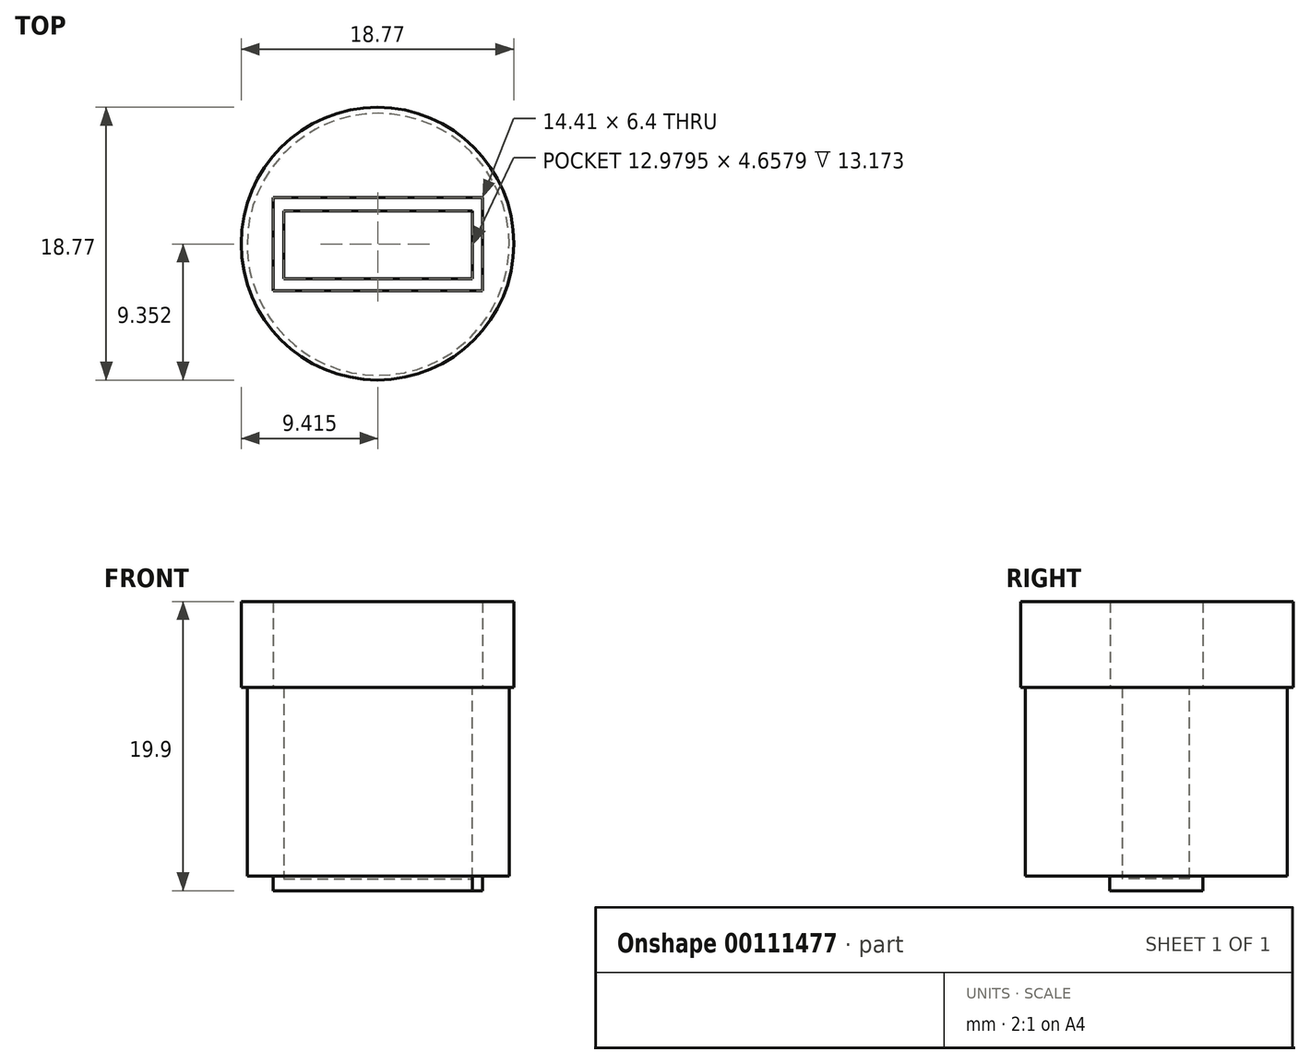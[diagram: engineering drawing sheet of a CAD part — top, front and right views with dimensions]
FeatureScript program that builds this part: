
annotation { "Feature Type Name" : "Feature", "Feature Type Description" : "" }
export const myFeature = defineFeature(function(context is Context, id is Id, definition is map)
    precondition{}
    {
        {
            var Q0;
            Q0=qCreatedBy(makeId("Top.planeOp"),FACE);
            var sketch = newSketch(context, id + "F0", { "sketchPlane" : qUnion([Q0])});
            skLineSegment(sketch, "E0.bottom", {"start": v(0, 0) * mm, "end": v(-14.41, 0) * mm});
            skLineSegment(sketch, "E0.top", {"start": v(0, -6.4) * mm, "end": v(-14.41, -6.4) * mm});
            skLineSegment(sketch, "E0.left", {"start": v(0, 0) * mm, "end": v(0, -6.4) * mm});
            skLineSegment(sketch, "E0.right", {"start": v(-14.41, 0) * mm, "end": v(-14.41, -6.4) * mm});
            skSolve(sketch);
        }
        {
            var Q0;
            Q0=makeQuery(id+"F0.imprint","IMPRINT",FACE,{"disambiguationData":[TD([[makeQuery(id+"F0.imprint","IMPRINT",EDGE,{"derivedFrom":sQuery(id+"F0.wireOp",EDGE,"E0.bottom")}),1.0]])]});
            var sketch = newSketch(context, id + "F1", { "sketchPlane" : qUnion([Q0])});
            skCircle(sketch, "E1", {"center": v(-7.23, -3.16) * mm, "radius": 9.39 * mm});
            skSolve(sketch);
        }
        {
            var Q0;
            Q0=makeQuery(id+"F1.imprint","IMPRINT",FACE,{"disambiguationData":[TD([[makeQuery(id+"F1.imprint","IMPRINT",EDGE,{"derivedFrom":sQuery(id+"F1.wireOp",EDGE,"E1")}),1.0]])]});
            extrude(context, id + "F2", {"entities" : qUnion([Q0]), "depth" : 5.9 * mm});
        }
        {
            var Q0;
            Q0=makeQuery(id+"F2.opExtrude","CAP_FACE",FACE,{"disambiguationData":[OSD([sQuery(id+"F0.wireOp",EDGE,"E0.bottom"),sQuery(id+"F0.wireOp",EDGE,"E0.top"),sQuery(id+"F0.wireOp",EDGE,"E0.left"),sQuery(id+"F0.wireOp",EDGE,"E0.right"),sQuery(id+"F1.wireOp",EDGE,"E1")])],"isStart":true});
            var sketch = newSketch(context, id + "F3", { "sketchPlane" : qUnion([Q0])});
            skLineSegment(sketch, "E2.bottom", {"start": v(0, 0) * mm, "end": v(-14.41, 0) * mm});
            skLineSegment(sketch, "E2.top", {"start": v(0, 0.92) * mm, "end": v(-14.41, 0.92) * mm});
            skLineSegment(sketch, "E2.left", {"start": v(0, 0) * mm, "end": v(0, 0.92) * mm});
            skLineSegment(sketch, "E2.right", {"start": v(-14.41, 0) * mm, "end": v(-14.41, 0.92) * mm});
            skSolve(sketch);
        }
        {
            var Q0;
            Q0=makeQuery(id+"F0.imprint","IMPRINT",FACE,{"disambiguationData":[TD([[makeQuery(id+"F0.imprint","IMPRINT",EDGE,{"derivedFrom":sQuery(id+"F0.wireOp",EDGE,"E0.bottom")}),1.0]])]});
            var sketch = newSketch(context, id + "F4", { "sketchPlane" : qUnion([Q0])});
            skCircle(sketch, "E3", {"center": v(-7.19, -3.2) * mm, "radius": 9.02 * mm});
            skSolve(sketch);
        }
        {
            var Q0;
            Q0=makeQuery(id+"F4.imprint","IMPRINT",FACE,{"disambiguationData":[TD([[makeQuery(id+"F4.imprint","IMPRINT",EDGE,{"derivedFrom":sQuery(id+"F4.wireOp",EDGE,"E3")}),1.0]])]});
            extrude(context, id + "F5", {"entities" : qUnion([Q0]), "operationType" : NewBodyOperationType.ADD, "oppositeDirection" : true, "depth" : 13 * mm});
        }
        {
            var Q0;
            Q0=makeQuery(id+"F3.imprint","IMPRINT",FACE,{"disambiguationData":[TD([[makeQuery(id+"F3.imprint","IMPRINT",EDGE,{"derivedFrom":sQuery(id+"F3.wireOp",EDGE,"E2.bottom")}),-1.0]])]});
            extrude(context, id + "F6", {"entities" : qUnion([Q0]), "operationType" : NewBodyOperationType.ADD, "depth" : 14 * mm});
        }
        {
            var Q0;
            Q0=makeQuery(id+"F6.opExtrude","SWEPT_FACE",FACE,{"disambiguationData":[OSD([sQuery(id+"F3.wireOp",EDGE,"E2.top")])]});
            var sketch = newSketch(context, id + "F7", { "sketchPlane" : qUnion([Q0])});
            skLineSegment(sketch, "E4.bottom", {"start": v(0, -14) * mm, "end": v(-0.7, -14) * mm});
            skLineSegment(sketch, "E4.top", {"start": v(0, 0) * mm, "end": v(-0.7, 0) * mm});
            skLineSegment(sketch, "E4.left", {"start": v(0, -14) * mm, "end": v(0, 0) * mm});
            skLineSegment(sketch, "E4.right", {"start": v(-0.7, -14) * mm, "end": v(-0.7, 0) * mm});
            skSolve(sketch);
        }
        {
            var Q0;
            {var subQ3=sQuery(id+"F7.wireOp",EDGE,"E4.bottom");Q0=makeQuery(id+"F7.imprint","IMPRINT",FACE,{"disambiguationData":[TD([[makeQuery(id+"F7.imprint","IMPRINT",EDGE,{"derivedFrom":subQ3}),-1.0]])]});}
            extrude(context, id + "F8", {"entities" : qUnion([Q0]), "operationType" : NewBodyOperationType.ADD, "depth" : 5.5 * mm});
        }
        {
            var Q0;
            Q0=makeQuery(id+"F8.opExtrude","SWEPT_FACE",FACE,{"disambiguationData":[OSD([sQuery(id+"F7.wireOp",EDGE,"E4.right")])]});
            var sketch = newSketch(context, id + "F9", { "sketchPlane" : qUnion([Q0])});
            skLineSegment(sketch, "E5.bottom", {"start": v(6.4, 0) * mm, "end": v(5.58, 0) * mm});
            skLineSegment(sketch, "E5.top", {"start": v(6.4, -14) * mm, "end": v(5.58, -14) * mm});
            skLineSegment(sketch, "E5.left", {"start": v(6.4, 0) * mm, "end": v(6.4, -14) * mm});
            skLineSegment(sketch, "E5.right", {"start": v(5.58, 0) * mm, "end": v(5.58, -14) * mm});
            skSolve(sketch);
        }
        {
            var Q0;
            {var subQ4=sQuery(id+"F9.wireOp",EDGE,"E5.bottom");Q0=makeQuery(id+"F9.imprint","IMPRINT",FACE,{"disambiguationData":[TD([[makeQuery(id+"F9.imprint","IMPRINT",EDGE,{"derivedFrom":subQ4}),1.0]])]});}
            extrude(context, id + "F10", {"entities" : qUnion([Q0]), "operationType" : NewBodyOperationType.ADD, "depth" : 13.7 * mm});
        }
        {
            var Q0;
            Q0=makeQuery(id+"F10.opExtrude","SWEPT_FACE",FACE,{"disambiguationData":[OSD([sQuery(id+"F9.wireOp",EDGE,"E5.right")])]});
            var sketch = newSketch(context, id + "F11", { "sketchPlane" : qUnion([Q0])});
            skLineSegment(sketch, "E6.bottom", {"start": v(14.4, -14) * mm, "end": v(13.68, -14) * mm});
            skLineSegment(sketch, "E6.top", {"start": v(14.4, 0) * mm, "end": v(13.68, 0) * mm});
            skLineSegment(sketch, "E6.left", {"start": v(14.4, -14) * mm, "end": v(14.4, 0) * mm});
            skLineSegment(sketch, "E6.right", {"start": v(13.68, -14) * mm, "end": v(13.68, 0) * mm});
            skSolve(sketch);
        }
        {
            var Q0;
            Q0=makeQuery(id+"F11.imprint","IMPRINT",FACE,{"disambiguationData":[TD([[makeQuery(id+"F11.imprint","IMPRINT",EDGE,{"derivedFrom":sQuery(id+"F11.wireOp",EDGE,"E6.bottom")}),-1.0]])]});
            extrude(context, id + "F12", {"entities" : qUnion([Q0]), "operationType" : NewBodyOperationType.ADD, "depth" : 5 * mm});
        }
        {
            var Q0;
            Q0=makeQuery(id+"F10.opExtrude","SWEPT_FACE",FACE,{"disambiguationData":[OSD([sQuery(id+"F9.wireOp",EDGE,"E5.right")])]});
            var sketch = newSketch(context, id + "F13", { "sketchPlane" : qUnion([Q0])});
            skLineSegment(sketch, "E7.bottom", {"start": v(0.7, -14) * mm, "end": v(13.68, -14) * mm});
            skLineSegment(sketch, "E7.top", {"start": v(0.7, -13.17) * mm, "end": v(13.68, -13.17) * mm});
            skLineSegment(sketch, "E7.left", {"start": v(0.7, -14) * mm, "end": v(0.7, -13.17) * mm});
            skLineSegment(sketch, "E7.right", {"start": v(13.68, -14) * mm, "end": v(13.68, -13.17) * mm});
            skSolve(sketch);
        }
        {
            var Q0;
            Q0=makeQuery(id+"F13.imprint","IMPRINT",FACE,{"disambiguationData":[TD([[makeQuery(id+"F13.imprint","IMPRINT",EDGE,{"derivedFrom":sQuery(id+"F13.wireOp",EDGE,"E7.bottom")}),-1.0]])]});
            extrude(context, id + "F14", {"entities" : qUnion([Q0]), "operationType" : NewBodyOperationType.ADD, "depth" : 5 * mm});
        }
    });
